# Revit family: 985400ARW OPAL CF EH WFCC 4S SUITE SF AR
name_source: partatom
category: Plumbing Fixtures
revit_build: Autodesk Revit 2016 (Build: 20161004_0715(x64)
units: mm (PartAtom-declared; Revit-internal decimal feet)

## family parameters
Cut with Voids When Loaded = No
Host = Face
OmniClass Number = 23.45.05.21.11.11
OmniClass Title = Water Operated Water Closets
Part Type = Normal
Room Calculation Point = No
Round Connector Dimension = Use Diameter
Shared = No

## types (1)
- OPAL CF EH WFCC 4S SUITE SF AR
    Assembly Code = D2010110
    CW Connection = Yes
    Default Elevation = 0 mm  [stored 0 ft]
    Description = OPAL CF EH WFCC 4S SUITE SF AR
    HW Connection = No
    Manufacturer = GWA Bathrooms & Kitchens
    Material_Arm = GWA_Metal-Stainless
    Material_Base = GWA_Metal-Chrome
    Material_Cistern = GWA-Porcelain-White
    Material_Handle = GWA-Acrylic-White
    Material_NC = GWA-Acrylic-Green
    Material_Seat = GWA-Acrylic-White
    Material_SeatDF = GWA-Acrylic-White
    Model = 985400ARW
    URL = https://www.caroma.com.au
    Vent Connection = No
    Waste Connection = Yes

note: [stored X ft] marks values corroborated as IEEE doubles in the binary element streams (Revit-internal decimal feet)

## geometry (parser evidence)
native form markers: Sweep x9
no freeform markers — native parametric forms only
